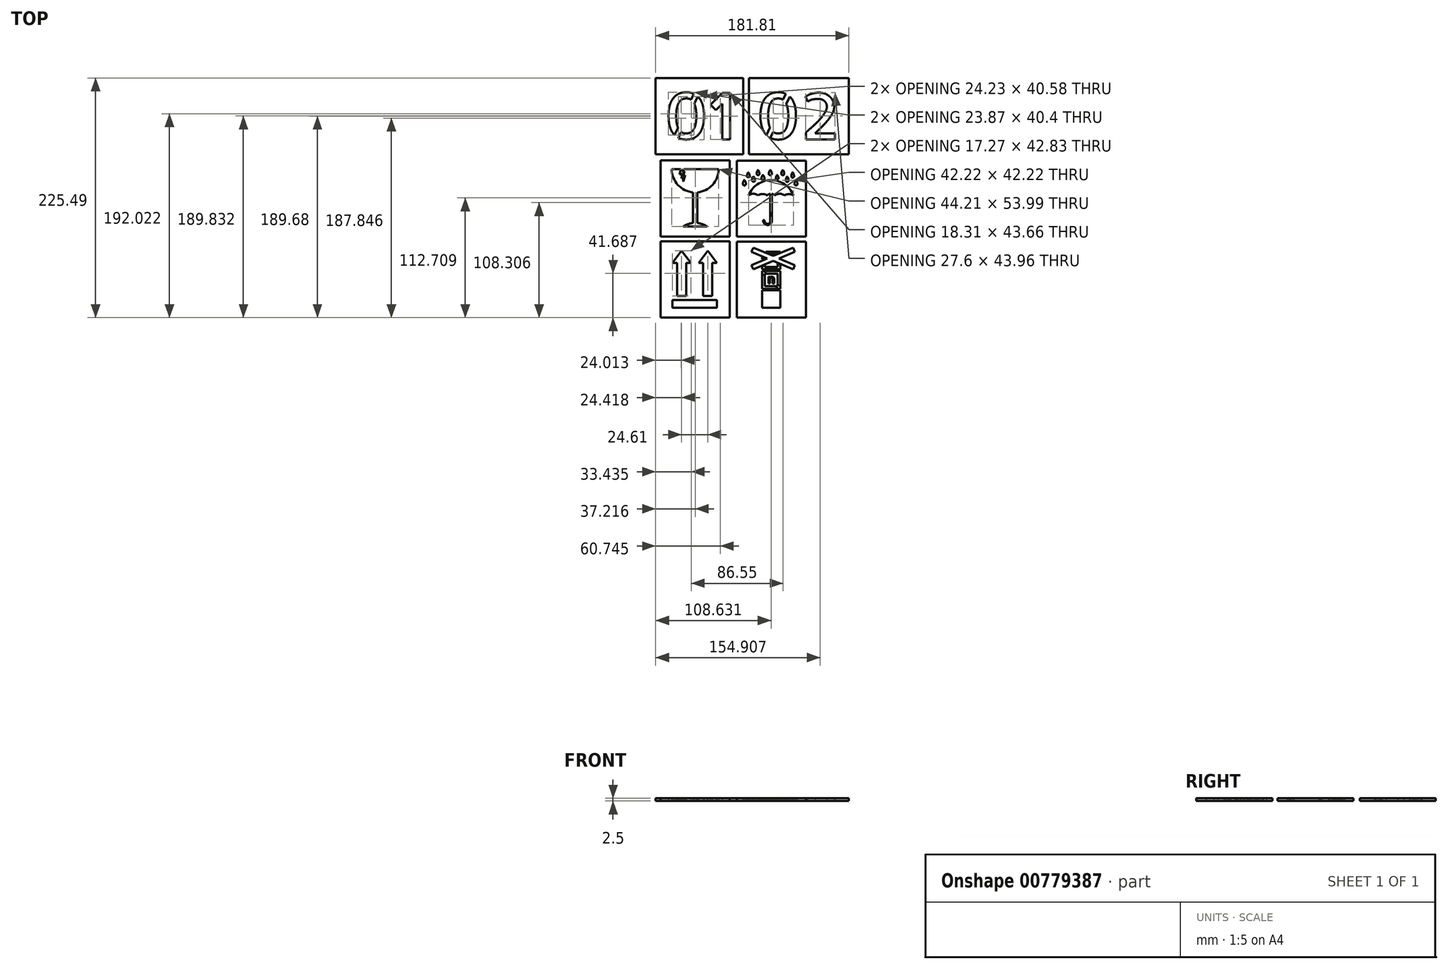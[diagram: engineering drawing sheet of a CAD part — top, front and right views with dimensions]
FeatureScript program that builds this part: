
annotation { "Feature Type Name" : "Feature", "Feature Type Description" : "" }
export const myFeature = defineFeature(function(context is Context, id is Id, definition is map)
    precondition{}
    {
        {
            var Q0;
            Q0=qCreatedBy(makeId("Top.planeOp"),FACE);
            var sketch = newSketch(context, id + "F0", { "sketchPlane" : qUnion([Q0])});
            skLineSegment(sketch, "E0.bottom", {"start": v(-70.03, -1.71) * mm, "end": v(-4.93, -1.71) * mm});
            skLineSegment(sketch, "E0.top", {"start": v(-70.03, -73.28) * mm, "end": v(-4.93, -73.28) * mm});
            skLineSegment(sketch, "E0.left", {"start": v(-70.03, -1.71) * mm, "end": v(-70.03, -73.28) * mm});
            skLineSegment(sketch, "E0.right", {"start": v(-4.93, -1.71) * mm, "end": v(-4.93, -73.28) * mm});
            skLineSegment(sketch, "E1", {"start": v(-50.27, -10.42) * mm, "end": v(-58.9, -22.02) * mm});
            skLineSegment(sketch, "E2", {"start": v(-58.9, -22.02) * mm, "end": v(-50.27, -22.02) * mm});
            skLineSegment(sketch, "E3", {"start": v(-50.27, -22.02) * mm, "end": v(-41.64, -22.02) * mm});
            skLineSegment(sketch, "E4", {"start": v(-25.66, -22.02) * mm, "end": v(-34.3, -22.02) * mm});
            skLineSegment(sketch, "E5", {"start": v(-25.66, -22.02) * mm, "end": v(-17.03, -22.02) * mm});
            skLineSegment(sketch, "E6", {"start": v(-25.66, -10.42) * mm, "end": v(-34.3, -22.02) * mm});
            skLineSegment(sketch, "E7", {"start": v(-50.27, -10.42) * mm, "end": v(-41.64, -22.02) * mm});
            skLineSegment(sketch, "E8", {"start": v(-25.66, -10.42) * mm, "end": v(-17.03, -22.02) * mm});
            skLineSegment(sketch, "E9", {"start": v(-54.6, -22.02) * mm, "end": v(-54.6, -53.25) * mm});
            skLineSegment(sketch, "E10", {"start": v(-45.95, -22.02) * mm, "end": v(-45.95, -53.25) * mm});
            skLineSegment(sketch, "E11", {"start": v(-45.95, -53.25) * mm, "end": v(-54.6, -53.25) * mm});
            skLineSegment(sketch, "E12", {"start": v(-29.98, -22.02) * mm, "end": v(-29.98, -53.25) * mm});
            skLineSegment(sketch, "E13", {"start": v(-29.98, -53.25) * mm, "end": v(-21.34, -53.25) * mm});
            skPoint(sketch, "E13.endSnap0", {"position": v(-21.34, -22.02) * mm});
            skLineSegment(sketch, "E14", {"start": v(-21.34, -53.25) * mm, "end": v(-21.34, -22.02) * mm});
            skLineSegment(sketch, "E15", {"start": v(-58.9, -57.01) * mm, "end": v(-17.03, -57.01) * mm});
            skLineSegment(sketch, "E16", {"start": v(-17.03, -57.01) * mm, "end": v(-17.03, -64.08) * mm});
            skLineSegment(sketch, "E17", {"start": v(-17.03, -64.08) * mm, "end": v(-58.9, -64.08) * mm});
            skLineSegment(sketch, "E18", {"start": v(-58.9, -64.08) * mm, "end": v(-58.9, -57.01) * mm});
            skSolve(sketch);
        }
        {
            var Q0;
            Q0=makeQuery(id+"F0.imprint","IMPRINT",FACE,{"disambiguationData":[TD([[makeQuery(id+"F0.imprint","IMPRINT",EDGE,{"derivedFrom":sQuery(id+"F0.wireOp",EDGE,"E0.bottom")}),-1.0]])]});
            extrude(context, id + "F1", {"entities" : qUnion([Q0]), "depth" : 2.5 * mm, "offsetDistance" : 25 * mm});
        }
        {
            var Q0;
            Q0=qCreatedBy(makeId("Top.planeOp"),FACE);
            var sketch = newSketch(context, id + "F2", { "sketchPlane" : qUnion([Q0])});
            skLineSegment(sketch, "E19.bottom", {"start": v(-70, 2.91) * mm, "end": v(-4.9, 2.91) * mm});
            skLineSegment(sketch, "E19.top", {"start": v(-70, 74.47) * mm, "end": v(-4.9, 74.47) * mm});
            skLineSegment(sketch, "E19.left", {"start": v(-70, 2.91) * mm, "end": v(-70, 74.47) * mm});
            skLineSegment(sketch, "E19.right", {"start": v(-4.9, 2.91) * mm, "end": v(-4.9, 74.47) * mm});
            skArc(sketch, "E20", {"start": v(-59.58, 66.18) * mm, "mid": v(-37.47, 44.3) * mm, "end": v(-15.37, 66.18) * mm});
            skLineSegment(sketch, "E21", {"start": v(-37.47, 44.3) * mm, "end": v(-37.45, 12.2) * mm});
            skLineSegment(sketch, "E22", {"start": v(-37.45, 12.2) * mm, "end": v(-37.46, 24.37) * mm});
            skLineSegment(sketch, "E23", {"start": v(-39.55, 44.4) * mm, "end": v(-39.52, 12.2) * mm});
            skLineSegment(sketch, "E24", {"start": v(-35.41, 44.4) * mm, "end": v(-35.41, 12.2) * mm});
            skArc(sketch, "E25", {"start": v(-26.36, 12.2) * mm, "mid": v(-37.53, 15.66) * mm, "end": v(-48.7, 12.2) * mm});
            skLineSegment(sketch, "E26", {"start": v(-48.7, 12.2) * mm, "end": v(-26.36, 12.2) * mm});
            skLineSegment(sketch, "E27", {"start": v(-50.9, 66.18) * mm, "end": v(-52.43, 61.35) * mm});
            skLineSegment(sketch, "E28", {"start": v(-52.43, 61.35) * mm, "end": v(-49.64, 62.03) * mm});
            skLineSegment(sketch, "E29", {"start": v(-49.64, 62.03) * mm, "end": v(-50.4, 57.64) * mm});
            skLineSegment(sketch, "E30", {"start": v(-50.4, 57.64) * mm, "end": v(-48.72, 58.32) * mm});
            skLineSegment(sketch, "E31", {"start": v(-48.72, 58.32) * mm, "end": v(-48.72, 54.6) * mm});
            skLineSegment(sketch, "E32", {"start": v(-48.72, 54.6) * mm, "end": v(-47.03, 60.43) * mm});
            skLineSegment(sketch, "E33", {"start": v(-47.03, 60.43) * mm, "end": v(-48.72, 59.58) * mm});
            skLineSegment(sketch, "E34", {"start": v(-48.72, 59.58) * mm, "end": v(-47.37, 64.24) * mm});
            skLineSegment(sketch, "E35", {"start": v(-47.37, 64.24) * mm, "end": v(-49.64, 63.63) * mm});
            skLineSegment(sketch, "E36", {"start": v(-49.64, 63.63) * mm, "end": v(-48.13, 66.18) * mm});
            skLineSegment(sketch, "E37", {"start": v(-50.9, 66.18) * mm, "end": v(-59.58, 66.18) * mm});
            skLineSegment(sketch, "E38", {"start": v(-48.13, 66.18) * mm, "end": v(-15.37, 66.18) * mm});
            skSolve(sketch);
        }
        {
            var Q0;
            Q0=makeQuery(id+"F2.imprint","IMPRINT",FACE,{"disambiguationData":[TD([[makeQuery(id+"F2.imprint","IMPRINT",EDGE,{"derivedFrom":sQuery(id+"F2.wireOp",EDGE,"E19.bottom")}),1.0]])]});
            extrude(context, id + "F3", {"entities" : qUnion([Q0]), "depth" : 2.5 * mm, "offsetDistance" : 25 * mm});
        }
        {
            var Q0;
            Q0=qCreatedBy(makeId("Top.planeOp"),FACE);
            var sketch = newSketch(context, id + "F4", { "sketchPlane" : qUnion([Q0])});
            skLineSegment(sketch, "E39.bottom", {"start": v(1.55, 74.36) * mm, "end": v(66.64, 74.36) * mm});
            skLineSegment(sketch, "E39.top", {"start": v(1.55, 2.85) * mm, "end": v(66.64, 2.85) * mm});
            skLineSegment(sketch, "E39.left", {"start": v(1.55, 74.36) * mm, "end": v(1.55, 2.85) * mm});
            skLineSegment(sketch, "E39.right", {"start": v(66.64, 74.36) * mm, "end": v(66.64, 2.85) * mm});
            skArc(sketch, "E40", {"start": v(55.05, 41.66) * mm, "mid": v(33.94, 55.9) * mm, "end": v(12.83, 41.66) * mm});
            skArc(sketch, "E41", {"start": v(55.05, 41.66) * mm, "mid": v(50.8, 42.72) * mm, "end": v(46.57, 41.66) * mm});
            skArc(sketch, "E42", {"start": v(21.63, 41.66) * mm, "mid": v(17.23, 43.06) * mm, "end": v(12.83, 41.66) * mm});
            skArc(sketch, "E43", {"start": v(30.22, 41.66) * mm, "mid": v(25.92, 42.93) * mm, "end": v(21.63, 41.66) * mm});
            skArc(sketch, "E44", {"start": v(46.57, 41.66) * mm, "mid": v(42.12, 43.1) * mm, "end": v(37.67, 41.66) * mm});
            skArc(sketch, "E45", {"start": v(37.67, 41.66) * mm, "mid": v(33.94, 43.05) * mm, "end": v(30.22, 41.66) * mm});
            skLineSegment(sketch, "E46", {"start": v(34.67, 43) * mm, "end": v(34.67, 17.41) * mm});
            skLineSegment(sketch, "E47", {"start": v(33.22, 43) * mm, "end": v(33.22, 17.41) * mm});
            skArc(sketch, "E48", {"start": v(30.43, 13.7) * mm, "mid": v(33.4, 14.6) * mm, "end": v(34.67, 17.41) * mm});
            skArc(sketch, "E49", {"start": v(26.45, 17.41) * mm, "mid": v(27.75, 14.81) * mm, "end": v(30.43, 13.7) * mm});
            skArc(sketch, "E50", {"start": v(30.43, 14.84) * mm, "mid": v(32.39, 15.51) * mm, "end": v(33.22, 17.41) * mm});
            skArc(sketch, "E51", {"start": v(27.85, 17.41) * mm, "mid": v(28.68, 15.66) * mm, "end": v(30.43, 14.84) * mm});
            skArc(sketch, "E52", {"start": v(27.85, 17.41) * mm, "mid": v(27.15, 18.32) * mm, "end": v(26.45, 17.41) * mm});
            skArc(sketch, "E53", {"start": v(7.35, 52) * mm, "mid": v(8.9, 50.87) * mm, "end": v(10.32, 52.15) * mm});
            skArc(sketch, "E54", {"start": v(10.32, 52.15) * mm, "mid": v(9.87, 54.32) * mm, "end": v(8.76, 56.23) * mm});
            skArc(sketch, "E55", {"start": v(8.76, 56.23) * mm, "mid": v(7.72, 54.23) * mm, "end": v(7.35, 52) * mm});
            skArc(sketch, "E56", {"start": v(16.11, 55.38) * mm, "mid": v(17.53, 54.37) * mm, "end": v(18.83, 55.53) * mm});
            skArc(sketch, "E57", {"start": v(24.97, 56.99) * mm, "mid": v(26.3, 56.12) * mm, "end": v(27.64, 56.94) * mm});
            skArc(sketch, "E58", {"start": v(38.47, 57.54) * mm, "mid": v(39.66, 56.62) * mm, "end": v(40.93, 57.44) * mm});
            skArc(sketch, "E59", {"start": v(47.88, 55.12) * mm, "mid": v(49.15, 54.3) * mm, "end": v(50.4, 55.17) * mm});
            skArc(sketch, "E60", {"start": v(56.08, 52) * mm, "mid": v(57.42, 50.86) * mm, "end": v(58.75, 52) * mm});
            skArc(sketch, "E61", {"start": v(11.28, 59.55) * mm, "mid": v(12.54, 58.48) * mm, "end": v(13.75, 59.6) * mm});
            skArc(sketch, "E62", {"start": v(20.4, 61.67) * mm, "mid": v(21.7, 60.6) * mm, "end": v(23.01, 61.67) * mm});
            skArc(sketch, "E63", {"start": v(31.82, 61.67) * mm, "mid": v(33.2, 60.54) * mm, "end": v(34.59, 61.67) * mm});
            skArc(sketch, "E64", {"start": v(43.65, 61.67) * mm, "mid": v(44.96, 60.46) * mm, "end": v(46.27, 61.67) * mm});
            skArc(sketch, "E65", {"start": v(53.06, 59.6) * mm, "mid": v(54.32, 58.24) * mm, "end": v(55.58, 59.6) * mm});
            skArc(sketch, "E66", {"start": v(12.39, 63.23) * mm, "mid": v(11.48, 61.5) * mm, "end": v(11.28, 59.55) * mm});
            skArc(sketch, "E67", {"start": v(13.75, 59.6) * mm, "mid": v(13.44, 61.56) * mm, "end": v(12.39, 63.23) * mm});
            skArc(sketch, "E68", {"start": v(17.27, 59.55) * mm, "mid": v(16.26, 57.59) * mm, "end": v(16.11, 55.38) * mm});
            skArc(sketch, "E69", {"start": v(18.83, 55.53) * mm, "mid": v(18.38, 57.67) * mm, "end": v(17.27, 59.55) * mm});
            skArc(sketch, "E70", {"start": v(21.7, 65.66) * mm, "mid": v(20.7, 63.78) * mm, "end": v(20.4, 61.67) * mm});
            skArc(sketch, "E71", {"start": v(23.01, 61.67) * mm, "mid": v(22.63, 63.76) * mm, "end": v(21.7, 65.66) * mm});
            skArc(sketch, "E72", {"start": v(26.29, 60.91) * mm, "mid": v(25.2, 59.1) * mm, "end": v(24.97, 56.99) * mm});
            skArc(sketch, "E73", {"start": v(27.64, 56.94) * mm, "mid": v(27.39, 59.07) * mm, "end": v(26.29, 60.91) * mm});
            skArc(sketch, "E74", {"start": v(33.2, 65.66) * mm, "mid": v(32.15, 63.8) * mm, "end": v(31.82, 61.67) * mm});
            skArc(sketch, "E75", {"start": v(34.59, 61.67) * mm, "mid": v(34.34, 63.82) * mm, "end": v(33.2, 65.66) * mm});
            skArc(sketch, "E76", {"start": v(39.6, 60.91) * mm, "mid": v(38.76, 59.32) * mm, "end": v(38.47, 57.54) * mm});
            skArc(sketch, "E77", {"start": v(40.93, 57.44) * mm, "mid": v(40.68, 59.34) * mm, "end": v(39.6, 60.91) * mm});
            skArc(sketch, "E78", {"start": v(45.04, 65.66) * mm, "mid": v(43.92, 63.82) * mm, "end": v(43.65, 61.67) * mm});
            skArc(sketch, "E79", {"start": v(46.27, 61.67) * mm, "mid": v(46.02, 63.78) * mm, "end": v(45.04, 65.66) * mm});
            skArc(sketch, "E80", {"start": v(49.15, 59.4) * mm, "mid": v(48.09, 57.39) * mm, "end": v(47.88, 55.12) * mm});
            skPoint(sketch, "E80.startSnap0", {"position": v(49.15, 54.3) * mm});
            skArc(sketch, "E81", {"start": v(50.4, 55.17) * mm, "mid": v(50.19, 57.4) * mm, "end": v(49.15, 59.4) * mm});
            skArc(sketch, "E82", {"start": v(54.27, 63.33) * mm, "mid": v(53.3, 61.58) * mm, "end": v(53.06, 59.6) * mm});
            skArc(sketch, "E83", {"start": v(55.58, 59.6) * mm, "mid": v(55.27, 61.6) * mm, "end": v(54.27, 63.33) * mm});
            skArc(sketch, "E84", {"start": v(57.24, 56.12) * mm, "mid": v(56.2, 54.2) * mm, "end": v(56.08, 52) * mm});
            skArc(sketch, "E85", {"start": v(58.75, 52) * mm, "mid": v(58.38, 54.2) * mm, "end": v(57.24, 56.12) * mm});
            skSolve(sketch);
        }
        {
            var Q0;
            Q0=makeQuery(id+"F4.imprint","IMPRINT",FACE,{"disambiguationData":[TD([[makeQuery(id+"F4.imprint","IMPRINT",EDGE,{"derivedFrom":sQuery(id+"F4.wireOp",EDGE,"E39.bottom")}),-1.0]])]});
            extrude(context, id + "F5", {"entities" : qUnion([Q0]), "depth" : 2.5 * mm, "offsetDistance" : 25 * mm});
        }
        {
            var Q0;
            Q0=qCreatedBy(makeId("Top.planeOp"),FACE);
            var sketch = newSketch(context, id + "F6", { "sketchPlane" : qUnion([Q0])});
            skLineSegment(sketch, "E86.bottom", {"start": v(1.58, -2) * mm, "end": v(66.67, -2) * mm});
            skLineSegment(sketch, "E86.top", {"start": v(1.58, -73.52) * mm, "end": v(66.67, -73.52) * mm});
            skLineSegment(sketch, "E86.left", {"start": v(1.58, -2) * mm, "end": v(1.58, -73.52) * mm});
            skLineSegment(sketch, "E86.right", {"start": v(66.67, -2) * mm, "end": v(66.67, -73.52) * mm});
            skPoint(sketch, "E87.endSnap0", {"position": v(34.12, -10.72) * mm});
            skLineSegment(sketch, "E88.bottom", {"start": v(25.63, -64.27) * mm, "end": v(42.61, -64.27) * mm});
            skLineSegment(sketch, "E88.top", {"start": v(25.63, -47.72) * mm, "end": v(42.61, -47.72) * mm});
            skLineSegment(sketch, "E88.left", {"start": v(25.63, -64.27) * mm, "end": v(25.63, -47.72) * mm});
            skLineSegment(sketch, "E88.right", {"start": v(42.61, -64.27) * mm, "end": v(42.61, -47.72) * mm});
            skLineSegment(sketch, "E89.bottom", {"start": v(42.61, -46.3) * mm, "end": v(25.63, -46.3) * mm});
            skLineSegment(sketch, "E89.top", {"start": v(42.61, -29.76) * mm, "end": v(25.63, -29.76) * mm});
            skLineSegment(sketch, "E89.left", {"start": v(42.61, -46.3) * mm, "end": v(42.61, -29.76) * mm});
            skLineSegment(sketch, "E89.right", {"start": v(25.63, -46.3) * mm, "end": v(25.63, -29.76) * mm});
            skLineSegment(sketch, "E90.bottom", {"start": v(25.63, -28.11) * mm, "end": v(42.61, -28.11) * mm});
            skLineSegment(sketch, "E90.top", {"start": v(25.63, -11.58) * mm, "end": v(42.61, -11.58) * mm});
            skLineSegment(sketch, "E90.left", {"start": v(25.63, -28.11) * mm, "end": v(25.63, -11.58) * mm});
            skLineSegment(sketch, "E90.right", {"start": v(42.61, -28.11) * mm, "end": v(42.61, -11.58) * mm});
            skLineSegment(sketch, "E91.bottom", {"start": v(28.14, -13.76) * mm, "end": v(40, -13.76) * mm});
            skLineSegment(sketch, "E91.top", {"start": v(28.14, -25.84) * mm, "end": v(40, -25.84) * mm});
            skLineSegment(sketch, "E91.left", {"start": v(28.14, -13.76) * mm, "end": v(28.14, -25.84) * mm});
            skLineSegment(sketch, "E91.right", {"start": v(40, -13.76) * mm, "end": v(40, -25.84) * mm});
            skLineSegment(sketch, "E92.bottom", {"start": v(28.14, -32.05) * mm, "end": v(40, -32.05) * mm});
            skLineSegment(sketch, "E92.top", {"start": v(28.14, -43.8) * mm, "end": v(40, -43.8) * mm});
            skLineSegment(sketch, "E92.left", {"start": v(28.14, -32.05) * mm, "end": v(28.14, -43.8) * mm});
            skLineSegment(sketch, "E92.right", {"start": v(40, -32.05) * mm, "end": v(40, -43.8) * mm});
            skText(sketch, "E93", { "text": "n", "fontName": "AllertaStencil-Regular.ttf"});
            skLineSegment(sketch, "E94", {"start": v(15.29, -11.58) * mm, "end": v(54.6, -28.11) * mm});
            skLineSegment(sketch, "E95", {"start": v(54.6, -28.11) * mm, "end": v(56.31, -24.06) * mm});
            skLineSegment(sketch, "E96", {"start": v(56.31, -24.06) * mm, "end": v(17.15, -7.6) * mm});
            skLineSegment(sketch, "E97", {"start": v(17.15, -7.6) * mm, "end": v(15.29, -11.58) * mm});
            skLineSegment(sketch, "E98", {"start": v(17.15, -28.11) * mm, "end": v(56.31, -11.58) * mm});
            skLineSegment(sketch, "E99", {"start": v(56.31, -11.58) * mm, "end": v(54.6, -7.55) * mm});
            skLineSegment(sketch, "E100", {"start": v(54.6, -7.55) * mm, "end": v(15.49, -24.06) * mm});
            skLineSegment(sketch, "E101", {"start": v(15.49, -24.06) * mm, "end": v(17.15, -28.11) * mm});
            skLineSegment(sketch, "E102", {"start": v(29.05, -11.58) * mm, "end": v(34.12, -13.76) * mm});
            skLineSegment(sketch, "E103", {"start": v(42.61, -11.58) * mm, "end": v(37.93, -13.76) * mm});
            skLineSegment(sketch, "E104", {"start": v(40, -22.75) * mm, "end": v(42.61, -23.91) * mm});
            skLineSegment(sketch, "E105", {"start": v(28.14, -24.23) * mm, "end": v(25.63, -25.4) * mm});
            skLineSegment(sketch, "E106", {"start": v(28.14, -17.92) * mm, "end": v(25.63, -16.92) * mm});
            skLineSegment(sketch, "E107", {"start": v(25.63, -18.47) * mm, "end": v(27.65, -17.72) * mm});
            skLineSegment(sketch, "E108", {"start": v(28.14, -33.94) * mm, "end": v(25.63, -32.05) * mm});
            skPoint(sketch, "E108.endSnap0", {"position": v(34.07, -32.05) * mm});
            skLineSegment(sketch, "E109", {"start": v(29.84, -32.05) * mm, "end": v(26.65, -29.76) * mm});
            skLineSegment(sketch, "E110", {"start": v(40, -42.27) * mm, "end": v(42.61, -44.3) * mm});
            skLineSegment(sketch, "E111", {"start": v(37.98, -43.8) * mm, "end": v(41.17, -46.3) * mm});
            const initialGuessF6  = {"E93": [0.03056, -0.04133, 1, 0, 0.00836]};
            skSetInitialGuess(sketch, initialGuessF6);
            skSolve(sketch);
        }
        {
            var Q0;
            Q0=makeQuery(id+"F6.imprint","IMPRINT",FACE,{"disambiguationData":[TD([[makeQuery(id+"F6.imprint","IMPRINT",EDGE,{"derivedFrom":sQuery(id+"F6.wireOp",EDGE,"E86.bottom")}),-1.0]])]});
            extrude(context, id + "F7", {"entities" : qUnion([Q0]), "depth" : 2.5 * mm, "offsetDistance" : 25 * mm});
        }
        {
            var Q0;
            {var subQ3=sQuery(id+"F6.wireOp",EDGE,"E107");Q0=makeQuery(id+"F6.imprint","IMPRINT",FACE,{"disambiguationData":[TD([[makeQuery(id+"F6.imprint","IMPRINT",EDGE,{"derivedFrom":subQ3}),-1.0]])]});}
            var Q1;
            {var subQ0=sQuery(id+"F6.wireOp",EDGE,"E106");var subQ5=sQuery(id+"F6.wireOp",EDGE,"E90.left");var subQ8=makeQuery(id+"F6.imprint","INTERSECT",VERTEX,{"derivedFrom":[subQ5,subQ0]});Q1=makeQuery(id+"F6.imprint","IMPRINT",FACE,{"disambiguationData":[TD([[makeQuery(id+"F6.imprint","IMPRINT",EDGE,{"disambiguationData":[TD([[subQ8,-1.0]])],"derivedFrom":subQ5}),-1.0]])]});}
            var Q2;
            {var subQ0=sQuery(id+"F6.wireOp",EDGE,"E102");Q2=makeQuery(id+"F6.imprint","IMPRINT",FACE,{"disambiguationData":[TD([[makeQuery(id+"F6.imprint","IMPRINT",EDGE,{"derivedFrom":subQ0}),-1.0]])]});}
            var Q3;
            {var subQ0=sQuery(id+"F6.wireOp",EDGE,"E103");Q3=makeQuery(id+"F6.imprint","IMPRINT",FACE,{"disambiguationData":[TD([[makeQuery(id+"F6.imprint","IMPRINT",EDGE,{"derivedFrom":subQ0}),1.0]])]});}
            var Q4;
            {var subQ0=sQuery(id+"F6.wireOp",EDGE,"E96");var subQ1=sQuery(id+"F6.wireOp",EDGE,"E90.right");var subQ2=makeQuery(id+"F6.imprint","INTERSECT",VERTEX,{"derivedFrom":[subQ1,subQ0]});Q4=makeQuery(id+"F6.imprint","IMPRINT",FACE,{"disambiguationData":[TD([[makeQuery(id+"F6.imprint","IMPRINT",EDGE,{"disambiguationData":[TD([[subQ2,-1.0]])],"derivedFrom":subQ1}),1.0]])]});}
            var Q5;
            {var subQ0=sQuery(id+"F6.wireOp",EDGE,"E104");Q5=makeQuery(id+"F6.imprint","IMPRINT",FACE,{"disambiguationData":[TD([[makeQuery(id+"F6.imprint","IMPRINT",EDGE,{"derivedFrom":subQ0}),1.0]])]});}
            var Q6;
            {var subQ0=sQuery(id+"F6.wireOp",EDGE,"E105");Q6=makeQuery(id+"F6.imprint","IMPRINT",FACE,{"disambiguationData":[TD([[makeQuery(id+"F6.imprint","IMPRINT",EDGE,{"derivedFrom":subQ0}),-1.0]])]});}
            var Q7;
            {var subQ0=sQuery(id+"F6.wireOp",EDGE,"E91.bottom");var subQ7=makeQuery(id+"F6.imprint","INTERSECT",VERTEX,{"derivedFrom":[subQ0,sQuery(id+"F6.wireOp",EDGE,"E102")]});Q7=makeQuery(id+"F6.imprint","IMPRINT",FACE,{"disambiguationData":[TD([[makeQuery(id+"F6.imprint","IMPRINT",EDGE,{"disambiguationData":[TD([[subQ7,1.0]])],"derivedFrom":subQ0}),-1.0]])]});}
            var Q8;
            {var subQ0=sQuery(id+"F6.wireOp",EDGE,"E91.left");var subQ1=makeQuery(id+"F6.imprint","INTERSECT",VERTEX,{"derivedFrom":[subQ0,sQuery(id+"F6.wireOp",EDGE,"E106")]});Q8=makeQuery(id+"F6.imprint","IMPRINT",FACE,{"disambiguationData":[TD([[makeQuery(id+"F6.imprint","IMPRINT",EDGE,{"disambiguationData":[TD([[subQ1,1.0]])],"derivedFrom":subQ0}),1.0]])]});}
            var Q9;
            {var subQ1=sQuery(id+"F6.wireOp",EDGE,"E91.top");Q9=makeQuery(id+"F6.imprint","IMPRINT",FACE,{"disambiguationData":[TD([[makeQuery(id+"F6.imprint","IMPRINT",EDGE,{"derivedFrom":subQ1}),1.0]])]});}
            extrude(context, id + "F8", {"entities" : qUnion([Q0, Q1, Q2, Q3, Q4, Q5, Q6, Q7, Q8, Q9]), "operationType" : NewBodyOperationType.ADD, "depth" : 2.5 * mm, "offsetDistance" : 25 * mm});
        }
        {
            var Q0;
            Q0=makeQuery(id+"F6.imprint","IMPRINT",FACE,{"disambiguationData":[TD([[makeQuery(id+"F6.imprint","IMPRINT",EDGE,{"derivedFrom":sQuery(id+"F6.wireOp",EDGE,"E92.bottom")}),-1.0]])]});
            extrude(context, id + "F9", {"entities" : qUnion([Q0]), "depth" : 2.5 * mm, "offsetDistance" : 25 * mm});
        }
        {
            var Q0;
            Q0=qCreatedBy(makeId("Top.planeOp"),FACE);
            var sketch = newSketch(context, id + "F10", { "sketchPlane" : qUnion([Q0])});
            skLineSegment(sketch, "E112.bottom", {"start": v(-74.7, 80.38) * mm, "end": v(7.82, 80.38) * mm});
            skLineSegment(sketch, "E112.top", {"start": v(-74.7, 151.97) * mm, "end": v(7.82, 151.97) * mm});
            skLineSegment(sketch, "E112.left", {"start": v(-74.7, 80.38) * mm, "end": v(-74.7, 151.97) * mm});
            skLineSegment(sketch, "E112.right", {"start": v(7.82, 80.38) * mm, "end": v(7.82, 151.97) * mm});
            skText(sketch, "E113", { "text": "01", "fontName": "AllertaStencil-Regular.ttf"});
            skLineSegment(sketch, "E114.bottom", {"start": v(13.08, 151.97) * mm, "end": v(107.12, 151.97) * mm});
            skLineSegment(sketch, "E114.top", {"start": v(13.08, 80.38) * mm, "end": v(107.12, 80.38) * mm});
            skLineSegment(sketch, "E114.left", {"start": v(13.08, 151.97) * mm, "end": v(13.08, 80.38) * mm});
            skLineSegment(sketch, "E114.right", {"start": v(107.12, 151.97) * mm, "end": v(107.12, 80.38) * mm});
            skText(sketch, "E115", { "text": "02", "fontName": "AllertaStencil-Regular.ttf"});
            const initialGuessF10  = {"E113": [-0.067, 0.09433, 1, 0, 0.04368], "E115": [0.01955, 0.09433, 1, 0, 0.04368]};
            skSetInitialGuess(sketch, initialGuessF10);
            skSolve(sketch);
        }
        {
            var Q0;
            Q0=makeQuery(id+"F10.imprint","IMPRINT",FACE,{"disambiguationData":[TD([[makeQuery(id+"F10.imprint","IMPRINT",EDGE,{"derivedFrom":sQuery(id+"F10.wireOp",EDGE,"E114.bottom")}),-1.0]])]});
            var Q1;
            Q1=makeQuery(id+"F10.imprint","IMPRINT",FACE,{"disambiguationData":[TD([[makeQuery(id+"F10.imprint","IMPRINT",EDGE,{"derivedFrom":sQuery(id+"F10.wireOp",EDGE,"E112.bottom")}),1.0]])]});
            extrude(context, id + "F11", {"entities" : qUnion([Q0, Q1]), "depth" : 2.5 * mm, "offsetDistance" : 25 * mm});
        }
        {
            var Q0;
            {var subQ3=sQuery(id+"F6.wireOp",EDGE,"E108");Q0=makeQuery(id+"F6.imprint","IMPRINT",FACE,{"disambiguationData":[TD([[makeQuery(id+"F6.imprint","IMPRINT",EDGE,{"derivedFrom":subQ3}),-1.0]])]});}
            var Q1;
            {var subQ3=sQuery(id+"F6.wireOp",EDGE,"E110");Q1=makeQuery(id+"F6.imprint","IMPRINT",FACE,{"disambiguationData":[TD([[makeQuery(id+"F6.imprint","IMPRINT",EDGE,{"derivedFrom":subQ3}),-1.0]])]});}
            extrude(context, id + "F12", {"entities" : qUnion([Q0, Q1]), "depth" : 2.5 * mm, "offsetDistance" : 25 * mm});
        }
    });
